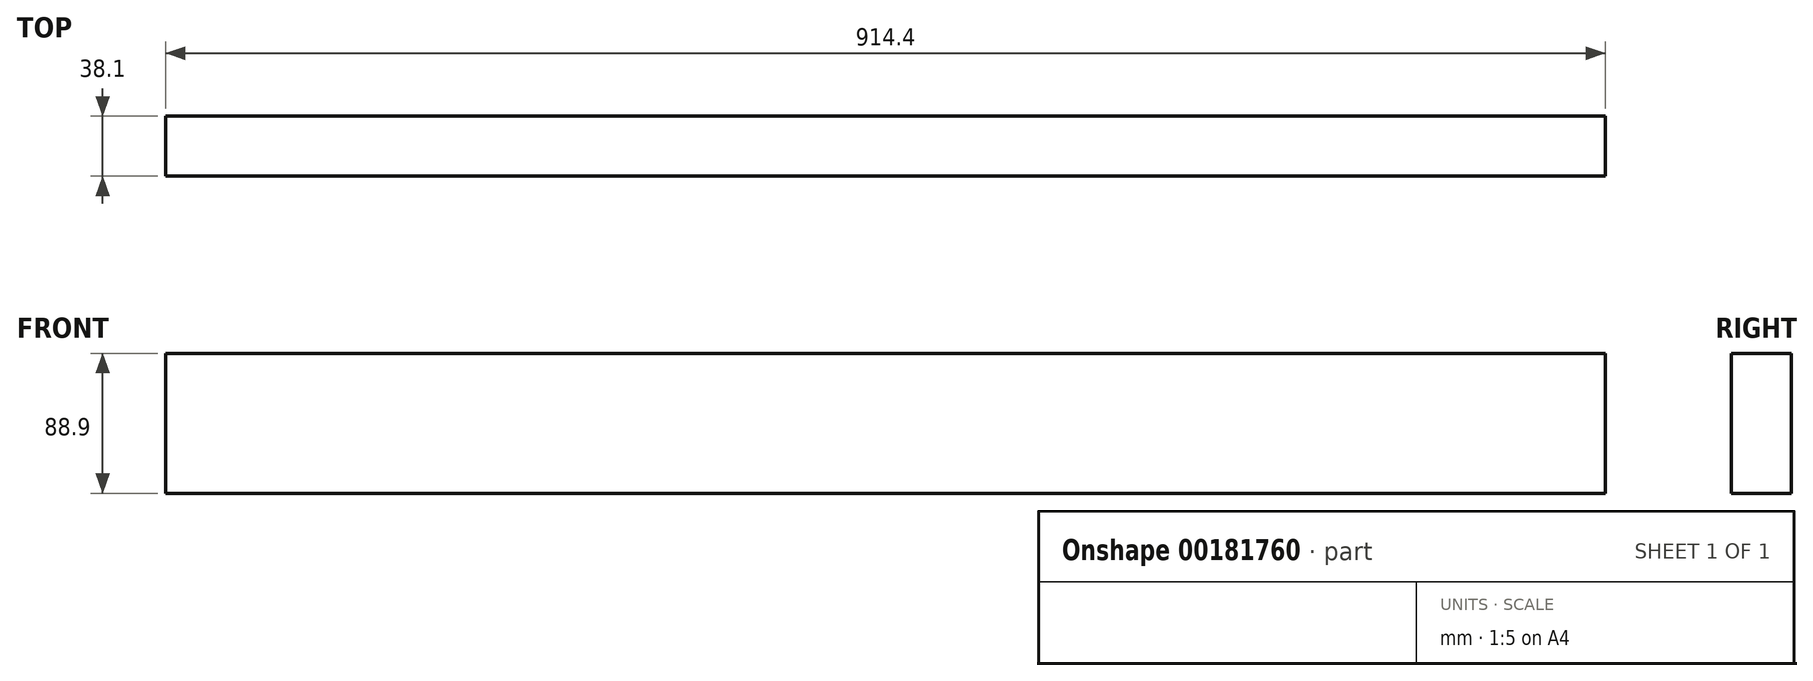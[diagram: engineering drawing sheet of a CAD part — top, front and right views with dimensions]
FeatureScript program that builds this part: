
annotation { "Feature Type Name" : "Feature", "Feature Type Description" : "" }
export const myFeature = defineFeature(function(context is Context, id is Id, definition is map)
    precondition{}
    {
        {
            var Q0;
            Q0=qCreatedBy(makeId("Front.planeOp"),FACE);
            var sketch = newSketch(context, id + "F0", { "sketchPlane" : qUnion([Q0])});
            skLineSegment(sketch, "E0.bottom", {"start": v(-454.5, 4.5) * mm, "end": v(459.9, 4.5) * mm});
            skLineSegment(sketch, "E0.top", {"start": v(-454.5, -84.4) * mm, "end": v(459.9, -84.4) * mm});
            skLineSegment(sketch, "E0.left", {"start": v(-454.5, 4.5) * mm, "end": v(-454.5, -84.4) * mm});
            skLineSegment(sketch, "E0.right", {"start": v(459.9, 4.5) * mm, "end": v(459.9, -84.4) * mm});
            skSolve(sketch);
        }
        {
            var Q0;
            Q0 = qSketchRegion(id + "F0", true);
            extrude(context, id + "F1", {"entities" : qUnion([Q0]), "depth" : 38.1 * mm});
        }
    });
